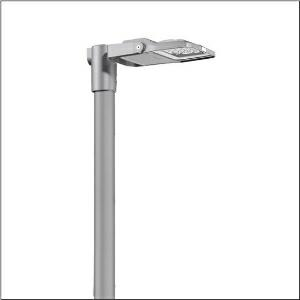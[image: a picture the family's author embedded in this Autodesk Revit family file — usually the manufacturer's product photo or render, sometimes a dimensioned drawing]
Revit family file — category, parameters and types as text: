
# Revit family: floodlight_fl_21_micro___pl43_5xa7762a4a3a_080e
name_source: partatom
category: Lighting Fixtures
units: mm (PartAtom-declared; Revit-internal decimal feet)

## family parameters
Cut with Voids When Loaded = No
Host = Face
Light Source = No
Part Type = Normal
Room Calculation Point = No
Round Connector Dimension = Use Diameter
Shared = No

## types (1)
- --- (1 x LED, 3170 lm, 23.1 W, 4000K)
    Apparent Load = 23 VA
    CIE Flux Codes = 29 80 99 100 100
    Color Rendering = 70
    Color Temperature = 4000K
    Default Elevation = 1800 mm
    Description = Floodlight FL 21 micro, floodlight, primary light control with lens, of PMMA, primary optical cover: protective disc, of toughened safety glass, transparent, light distribution: PL43, light emission: direct distribution, installation type: surface-mounted, LED, High Power LED, rated luminous flux: 3.170lm, luminous efficacy: 137lm/W, light colour: 740, colour temperature: 4000K, control gear: ECG iQ, control: Auto-Match, Temp-Guard, Night-Set, Smart-Wire, Desk-Remote (wireless, voltage-free reading and setting of iQ features in the workshop via application-optimized NFC function/RFID function), optimised constant luminous flux control (CLO 2.0), Street-Remote, with terminal, 6-pole, mains connection: 220..240V, AC, 50/60Hz, start of lifetime: 23W, end of lifetime: 34W, reduction: 11W, luminaire housing, of diecast aluminium, powder-coated, Siteco® metallic grey (DB 702S), corrosivity category C5 according to DIN EN ISO 12944, mast bracket, of steel, galvanised, powder-coated, Siteco® metallic grey (DB 702S), protection rating (complete): IP66, insulation class (complete): insulation class II (safety insulation), certification: CE, protection symbol: D, impact resistance: IK07, permissible operating ambient temperature: -40..+40°C, permissible operating ambient temperature for outdoor applications: -40..+50°C, standard: DIN EN 12944, packaging unit: 1 piece

Light Distribution: PL43
    Height = 65 mm
    Lamp = 1 x LED
    Lamp Light Flux = 3170 lm
    Lamp Power = 23.1 W
    Lamp count = 1
    Length = 312 mm
    Luminous efficacy = 137 lm/W
    Manufacturer = Siteco
    ModVariant = No
    Model = 5XA7762A4A3A
    Number of Poles = 1
    OnlyDefault = Yes
    Power Factor = 1
    Product Name = Floodlight FL 21 micro | PL43
    Product group = floodlight | pylon top
    ProductGroupID = 6101
    Protection Class = Protection class II
    Protection Degree = IP 66
    RLX_Detail_Level = 1
    RlxData = <blob elided: 101573 chars, md5=b6f11b8e>
    Socket = socket
    Standby Power = 0 W
    System Light Flux = 3170 lm
    System Power = 23 W
    Type Comments = factory setting: luminous flux: 100 % | dim-lin: 254 | 455 mA
    Type Image = l_1007121.jpg
    URL = http://relux.com
    VarID = @adj_089749
    Voltage = 0 V
    Weight = 0.00 kg
    Width = 230 mm

## geometry (parser evidence)
native form markers: Blend x4, Sweep x12
no freeform markers — native parametric forms only
